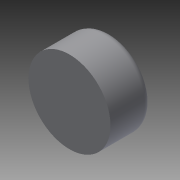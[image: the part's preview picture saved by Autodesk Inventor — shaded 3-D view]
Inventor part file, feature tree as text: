
AUTODESK INVENTOR PART (.ipt)
format: ipt  version: 2015 (Build 190159000, 159)  size: 94,720 bytes
history: native  units: mm
features: extrude x1, fillet x1, sketch x1
ambient origin geometry x8: Origin, YZ Plane, XZ Plane, XY Plane, X Axis, Y Axis, Z Axis, Center Point
bodies: Solid1 (feature_tree)
feature tree (3):
  extrude  "Extrusion1"  Depth=6.0mm TaperAngle=0.0deg
  fillet  "Fillet1"  Radius=1.0mm
  sketch  "Sketch1"  dims[d0=12.0mm d1=6.0mm d2=0.0mm d3=1.0mm]
